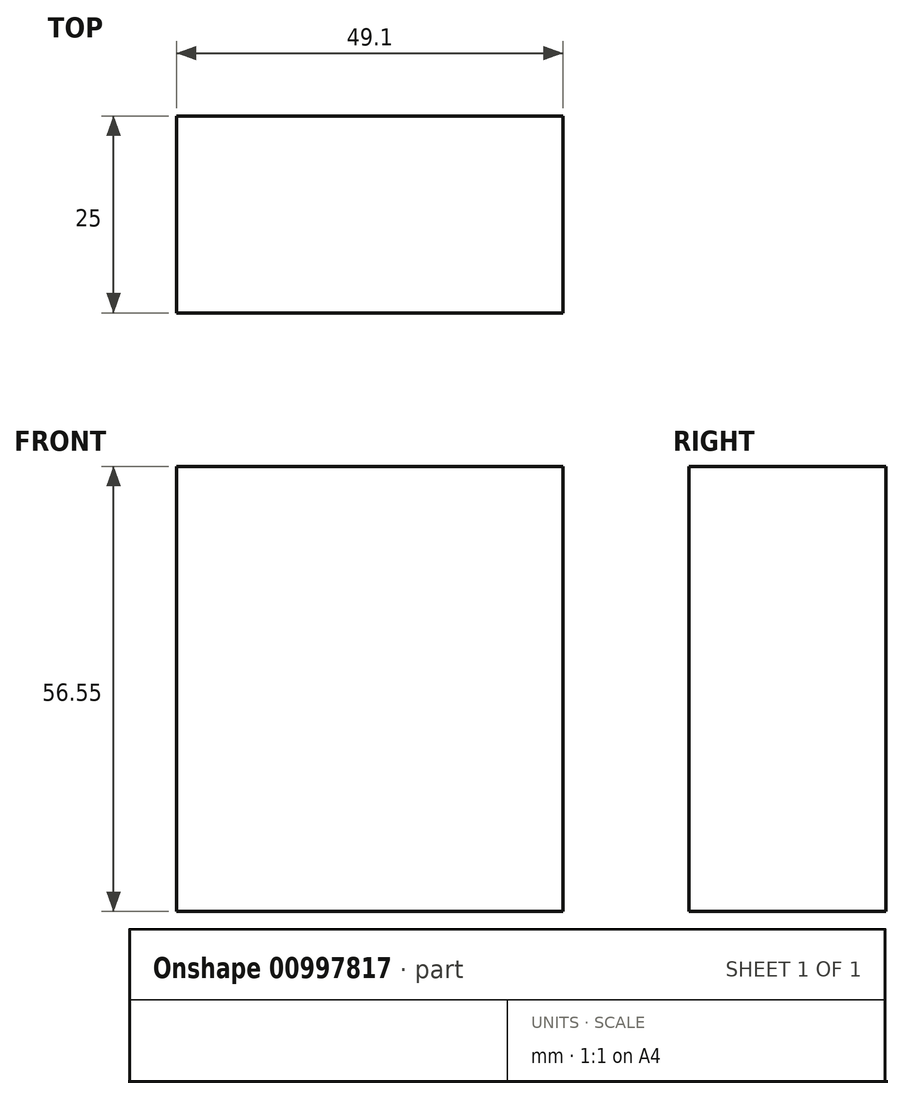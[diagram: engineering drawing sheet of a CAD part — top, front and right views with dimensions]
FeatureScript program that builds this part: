
annotation { "Feature Type Name" : "Feature", "Feature Type Description" : "" }
export const myFeature = defineFeature(function(context is Context, id is Id, definition is map)
    precondition{}
    {
        {
            var Q0;
            Q0=qCreatedBy(makeId("Front.planeOp"),FACE);
            var sketch = newSketch(context, id + "F0", { "sketchPlane" : qUnion([Q0])});
            skLineSegment(sketch, "E0.bottom", {"start": v(-122, 29.22) * mm, "end": v(-72.91, 29.22) * mm});
            skLineSegment(sketch, "E0.top", {"start": v(-122, -27.33) * mm, "end": v(-72.91, -27.33) * mm});
            skLineSegment(sketch, "E0.left", {"start": v(-122, 29.22) * mm, "end": v(-122, -27.33) * mm});
            skLineSegment(sketch, "E0.right", {"start": v(-72.91, 29.22) * mm, "end": v(-72.91, -27.33) * mm});
            skSolve(sketch);
        }
        {
            var Q0;
            Q0 = qSketchRegion(id + "F0", true);
            extrude(context, id + "F1", {"entities" : qUnion([Q0]), "depth" : 25 * mm, "offsetDistance" : 25 * mm});
        }
    });
